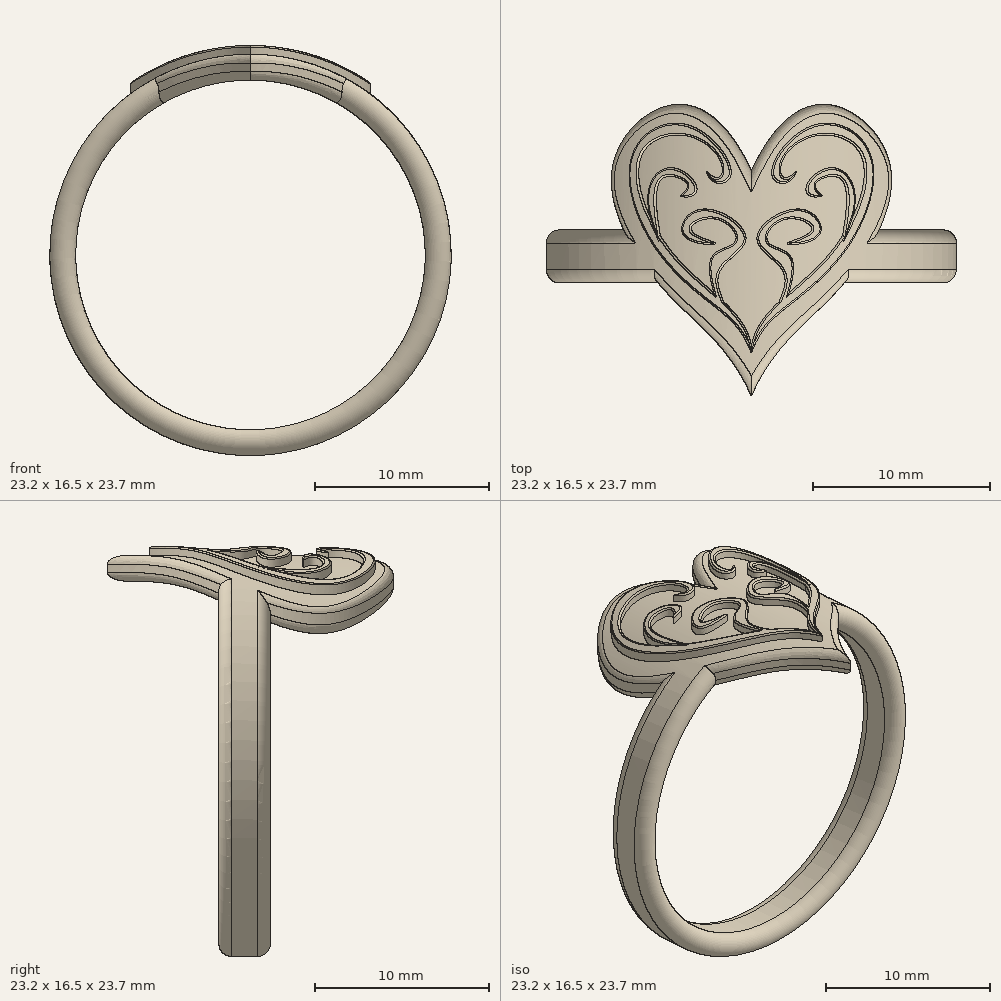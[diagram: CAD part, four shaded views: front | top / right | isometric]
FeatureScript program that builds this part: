
annotation { "Feature Type Name" : "Feature", "Feature Type Description" : "" }
export const myFeature = defineFeature(function(context is Context, id is Id, definition is map)
    precondition{}
    {
        {
            var Q0;
            Q0=qCreatedBy(makeId("Top.planeOp"),FACE);
            var sketch = newSketch(context, id + "F0", { "sketchPlane" : qUnion([Q0])});
            skFitSpline(sketch, "E0", {"points": [v(0, 4.84) * mm, v(-4.43, 8.58) * mm, v(-7.87, 5.02) * mm, v(-5.4, -1.36) * mm, v(-1.9, -4.93) * mm, v(0, -7.93) * mm], "startDerivative": vector(-17.19, 37.33) * mm, "endDerivative": vector(6.53, -16.13) * mm});
            skFitSpline(sketch, "E1.MirrorCS", {"points": [v(0, 4.84) * mm, v(4.43, 8.58) * mm, v(7.87, 5.02) * mm, v(5.4, -1.36) * mm, v(1.9, -4.93) * mm, v(0, -7.93) * mm], "startDerivative": vector(17.19, 37.33) * mm, "endDerivative": vector(-6.53, -16.13) * mm});
            skSolve(sketch);
        }
        {
            var Q0;
            Q0=qSketchRegion(id+"F0",true);
            extrude(context, id + "F1", {"entities" : qUnion([Q0]), "depth" : 19.05 * mm, "offsetDistance" : 25.4 * mm});
        }
        {
            var Q0;
            Q0=qCreatedBy(makeId("Front.planeOp"),FACE);
            var sketch = newSketch(context, id + "F2", { "sketchPlane" : qUnion([Q0])});
            skCircle(sketch, "E2", {"center": v(0, 0) * mm, "radius": 10.1 * mm});
            skCircle(sketch, "E3", {"center": v(0, 0) * mm, "radius": 11.6 * mm});
            skCircle(sketch, "E4", {"center": v(0, 0) * mm, "radius": 23.1 * mm});
            skCircle(sketch, "E5", {"center": v(0, 0) * mm, "radius": 12.1 * mm});
            skSolve(sketch);
        }
        {
            var Q0;
            Q0=makeQuery(id+"F2.imprint","IMPRINT",FACE,{"disambiguationData":[TD([[makeQuery(id+"F2.imprint","IMPRINT",EDGE,{"derivedFrom":sQuery(id+"F2.wireOp",EDGE,"E2")}),1.0]])]});
            extrude(context, id + "F3", {"entities" : qUnion([Q0]), "operationType" : NewBodyOperationType.REMOVE, "endBound" : BoundingType.SYMMETRIC, "oppositeDirection" : true, "depth" : 25.4 * mm, "offsetDistance" : 25.4 * mm});
        }
        {
            var Q0;
            Q0=makeQuery(id+"F2.imprint","IMPRINT",FACE,{"disambiguationData":[TD([[makeQuery(id+"F2.imprint","IMPRINT",EDGE,{"derivedFrom":sQuery(id+"F2.wireOp",EDGE,"J1NiXKZb-P4VB-i30b-1DHM-Y5gP9JKZlhvH")}),-1.0]])]});
            var Q1;
            Q1=makeQuery(id+"F2.imprint","IMPRINT",FACE,{"disambiguationData":[TD([[makeQuery(id+"F2.imprint","IMPRINT",EDGE,{"derivedFrom":sQuery(id+"F2.wireOp",EDGE,"E3")}),-1.0]])]});
            var Q2;
            Q2=makeQuery(id+"F2.imprint","IMPRINT",FACE,{"disambiguationData":[TD([[makeQuery(id+"F2.imprint","IMPRINT",EDGE,{"derivedFrom":sQuery(id+"F2.wireOp",EDGE,"E4")}),1.0]])]});
            extrude(context, id + "F4", {"entities" : qUnion([Q0, Q1, Q2]), "operationType" : NewBodyOperationType.REMOVE, "endBound" : BoundingType.SYMMETRIC, "oppositeDirection" : true, "depth" : 25.4 * mm, "offsetDistance" : 25.4 * mm});
        }
        {
            var Q0;
            Q0=makeQuery(id+"F2.imprint","IMPRINT",FACE,{"disambiguationData":[TD([[makeQuery(id+"F2.imprint","IMPRINT",EDGE,{"derivedFrom":sQuery(id+"F2.wireOp",EDGE,"E2")}),-1.0]])]});
            extrude(context, id + "F5", {"entities" : qUnion([Q0]), "operationType" : NewBodyOperationType.ADD, "endBound" : BoundingType.SYMMETRIC, "oppositeDirection" : true, "depth" : 3 * mm, "offsetDistance" : 25.4 * mm});
        }
        {
            var Q0;
            Q0=makeQuery(id+"F5.opExtrude","CAP_EDGE",EDGE,{"disambiguationData":[OSD([sQuery(id+"F2.wireOp",EDGE,"E3")])],"isStart":false});
            var Q1;
            Q1=makeQuery(id+"F5.opExtrude","CAP_EDGE",EDGE,{"disambiguationData":[OSD([sQuery(id+"F2.wireOp",EDGE,"E3")])],"isStart":true});
            var Q2;
            Q2=makeQuery(id+"F5.opExtrude","CAP_EDGE",EDGE,{"disambiguationData":[OSD([sQuery(id+"F2.wireOp",EDGE,"E2")])],"isStart":true});
            var Q3;
            Q3=makeQuery(id+"F5.opExtrude","CAP_EDGE",EDGE,{"disambiguationData":[OSD([sQuery(id+"F2.wireOp",EDGE,"E2")])],"isStart":false});
            fillet(context, id + "F6", {"entities" : qUnion([Q0, Q1, Q2, Q3]), "radius" : 0.75 * mm, "tangentPropagation" : true, "allowEdgeOverflow" : false});
        }
        {
            var Q0;
            {var subQ0=sQuery(id+"F2.wireOp",EDGE,"E2");Q0=makeQuery(id+"F3vgbqmcV8FAg6H_1.boolean.opBoolean","INTERSECT",EDGE,{"derivedFrom":[makeQuery(id+"F5.boolean.opBoolean","MERGE",FACE,{"derivedFrom":[makeQuery(id+"F3.boolean.opBoolean","COPY",FACE,{"derivedFrom":makeQuery(id+"F3.opExtrude","SWEPT_FACE",FACE,{"disambiguationData":[OSD([subQ0])]})}),makeQuery(id+"F5.opExtrude","SWEPT_FACE",FACE,{"disambiguationData":[OSD([subQ0])]})]}),makeQuery(id+"F3vgbqmcV8FAg6H_1.opExtrude","SWEPT_FACE",FACE,{"disambiguationData":[OSD([sQuery(id+"FdaOgL3yxnfuasM_1.wireOp",EDGE,"7c5b9e70-dd16-4398-a68a-3725518f416c")])]})]});}
            var Q1;
            {var subQ0=sQuery(id+"F2.wireOp",EDGE,"E3");Q1=makeQuery(id+"F3vgbqmcV8FAg6H_1.boolean.opBoolean","INTERSECT",EDGE,{"derivedFrom":[makeQuery(id+"F5.boolean.opBoolean","MERGE",FACE,{"derivedFrom":[makeQuery(id+"F4.boolean.opBoolean","COPY",FACE,{"derivedFrom":makeQuery(id+"F4.opExtrude","SWEPT_FACE",FACE,{"disambiguationData":[OSD([subQ0])]})}),makeQuery(id+"F5.opExtrude","SWEPT_FACE",FACE,{"disambiguationData":[OSD([subQ0])]})]}),makeQuery(id+"F3vgbqmcV8FAg6H_1.opExtrude","SWEPT_FACE",FACE,{"disambiguationData":[OSD([sQuery(id+"FdaOgL3yxnfuasM_1.wireOp",EDGE,"b2f0029b-c6ea-482f-b3c2-dee7be65e3070.MirrorCS")])]})]});}
            var Q2;
            {var subQ0=sQuery(id+"F2.wireOp",EDGE,"E2");Q2=makeQuery(id+"F3vgbqmcV8FAg6H_1.boolean.opBoolean","INTERSECT",EDGE,{"derivedFrom":[makeQuery(id+"F5.boolean.opBoolean","MERGE",FACE,{"derivedFrom":[makeQuery(id+"F3.boolean.opBoolean","COPY",FACE,{"derivedFrom":makeQuery(id+"F3.opExtrude","SWEPT_FACE",FACE,{"disambiguationData":[OSD([subQ0])]})}),makeQuery(id+"F5.opExtrude","SWEPT_FACE",FACE,{"disambiguationData":[OSD([subQ0])]})]}),makeQuery(id+"F3vgbqmcV8FAg6H_1.opExtrude","SWEPT_FACE",FACE,{"disambiguationData":[OSD([sQuery(id+"FdaOgL3yxnfuasM_1.wireOp",EDGE,"b2f0029b-c6ea-482f-b3c2-dee7be65e3070.MirrorCS")])]})]});}
            var Q3;
            {var subQ0=sQuery(id+"F2.wireOp",EDGE,"E3");Q3=makeQuery(id+"F3vgbqmcV8FAg6H_1.boolean.opBoolean","INTERSECT",EDGE,{"derivedFrom":[makeQuery(id+"F5.boolean.opBoolean","MERGE",FACE,{"derivedFrom":[makeQuery(id+"F4.boolean.opBoolean","COPY",FACE,{"derivedFrom":makeQuery(id+"F4.opExtrude","SWEPT_FACE",FACE,{"disambiguationData":[OSD([subQ0])]})}),makeQuery(id+"F5.opExtrude","SWEPT_FACE",FACE,{"disambiguationData":[OSD([subQ0])]})]}),makeQuery(id+"F3vgbqmcV8FAg6H_1.opExtrude","SWEPT_FACE",FACE,{"disambiguationData":[OSD([sQuery(id+"FdaOgL3yxnfuasM_1.wireOp",EDGE,"7c5b9e70-dd16-4398-a68a-3725518f416c")])]})]});}
            var Q4;
            {var subQ0=sQuery(id+"F2.wireOp",EDGE,"E3");var subQ1=makeQuery(id+"F4.opExtrude","SWEPT_FACE",FACE,{"disambiguationData":[OSD([subQ0])]});var subQ2=makeQuery(id+"F1.opExtrude","SWEPT_FACE",FACE,{"disambiguationData":[OSD([sQuery(id+"F0.wireOp",EDGE,"E0")])]});Q4=makeQuery(id+"F5.boolean.opBoolean","SPLIT",EDGE,{"disambiguationData":[TD([makeQuery(id+"F5.opExtrude","CAP_FACE",FACE,{"disambiguationData":[OSD([sQuery(id+"F2.wireOp",EDGE,"E2"),subQ0])],"isStart":false})])],"derivedFrom":makeQuery(id+"F4.boolean.opBoolean","INTERSECT",EDGE,{"derivedFrom":[subQ2,subQ1]})});}
            var Q5;
            {var subQ0=sQuery(id+"F2.wireOp",EDGE,"E3");var subQ1=makeQuery(id+"F4.opExtrude","SWEPT_FACE",FACE,{"disambiguationData":[OSD([subQ0])]});var subQ2=makeQuery(id+"F1.opExtrude","SWEPT_FACE",FACE,{"disambiguationData":[OSD([sQuery(id+"F0.wireOp",EDGE,"E1.MirrorCS")])]});Q5=makeQuery(id+"F5.boolean.opBoolean","SPLIT",EDGE,{"disambiguationData":[TD([makeQuery(id+"F5.opExtrude","CAP_FACE",FACE,{"disambiguationData":[OSD([sQuery(id+"F2.wireOp",EDGE,"E2"),subQ0])],"isStart":false})])],"derivedFrom":makeQuery(id+"F4.boolean.opBoolean","INTERSECT",EDGE,{"derivedFrom":[subQ2,subQ1]})});}
            var Q6;
            {var subQ0=sQuery(id+"F2.wireOp",EDGE,"E3");var subQ1=makeQuery(id+"F4.opExtrude","SWEPT_FACE",FACE,{"disambiguationData":[OSD([subQ0])]});var subQ2=makeQuery(id+"F1.opExtrude","SWEPT_FACE",FACE,{"disambiguationData":[OSD([sQuery(id+"F0.wireOp",EDGE,"E1.MirrorCS")])]});Q6=makeQuery(id+"F5.boolean.opBoolean","SPLIT",EDGE,{"disambiguationData":[TD([makeQuery(id+"F5.opExtrude","CAP_FACE",FACE,{"disambiguationData":[OSD([sQuery(id+"F2.wireOp",EDGE,"E2"),subQ0])],"isStart":true})])],"derivedFrom":makeQuery(id+"F4.boolean.opBoolean","INTERSECT",EDGE,{"derivedFrom":[subQ2,subQ1]})});}
            var Q7;
            {var subQ0=sQuery(id+"F2.wireOp",EDGE,"E3");var subQ1=makeQuery(id+"F4.opExtrude","SWEPT_FACE",FACE,{"disambiguationData":[OSD([subQ0])]});var subQ2=makeQuery(id+"F1.opExtrude","SWEPT_FACE",FACE,{"disambiguationData":[OSD([sQuery(id+"F0.wireOp",EDGE,"E0")])]});Q7=makeQuery(id+"F5.boolean.opBoolean","SPLIT",EDGE,{"disambiguationData":[TD([makeQuery(id+"F5.opExtrude","CAP_FACE",FACE,{"disambiguationData":[OSD([sQuery(id+"F2.wireOp",EDGE,"E2"),subQ0])],"isStart":true})])],"derivedFrom":makeQuery(id+"F4.boolean.opBoolean","INTERSECT",EDGE,{"derivedFrom":[subQ2,subQ1]})});}
            var Q8;
            {var subQ0=sQuery(id+"F2.wireOp",EDGE,"E2");var subQ1=makeQuery(id+"F3.opExtrude","SWEPT_FACE",FACE,{"disambiguationData":[OSD([subQ0])]});var subQ2=makeQuery(id+"F1.opExtrude","SWEPT_FACE",FACE,{"disambiguationData":[OSD([sQuery(id+"F0.wireOp",EDGE,"E0")])]});Q8=makeQuery(id+"F5.boolean.opBoolean","SPLIT",EDGE,{"disambiguationData":[TD([makeQuery(id+"F5.opExtrude","CAP_FACE",FACE,{"disambiguationData":[OSD([subQ0,sQuery(id+"F2.wireOp",EDGE,"E3")])],"isStart":true})])],"derivedFrom":makeQuery(id+"F3.boolean.opBoolean","INTERSECT",EDGE,{"derivedFrom":[subQ2,subQ1]})});}
            var Q9;
            {var subQ0=sQuery(id+"F2.wireOp",EDGE,"E2");var subQ1=makeQuery(id+"F3.opExtrude","SWEPT_FACE",FACE,{"disambiguationData":[OSD([subQ0])]});var subQ2=makeQuery(id+"F1.opExtrude","SWEPT_FACE",FACE,{"disambiguationData":[OSD([sQuery(id+"F0.wireOp",EDGE,"E1.MirrorCS")])]});Q9=makeQuery(id+"F5.boolean.opBoolean","SPLIT",EDGE,{"disambiguationData":[TD([makeQuery(id+"F5.opExtrude","CAP_FACE",FACE,{"disambiguationData":[OSD([subQ0,sQuery(id+"F2.wireOp",EDGE,"E3")])],"isStart":true})])],"derivedFrom":makeQuery(id+"F3.boolean.opBoolean","INTERSECT",EDGE,{"derivedFrom":[subQ2,subQ1]})});}
            var Q10;
            {var subQ0=sQuery(id+"F2.wireOp",EDGE,"E2");var subQ1=makeQuery(id+"F3.opExtrude","SWEPT_FACE",FACE,{"disambiguationData":[OSD([subQ0])]});var subQ2=makeQuery(id+"F1.opExtrude","SWEPT_FACE",FACE,{"disambiguationData":[OSD([sQuery(id+"F0.wireOp",EDGE,"E0")])]});Q10=makeQuery(id+"F5.boolean.opBoolean","SPLIT",EDGE,{"disambiguationData":[TD([makeQuery(id+"F5.opExtrude","CAP_FACE",FACE,{"disambiguationData":[OSD([subQ0,sQuery(id+"F2.wireOp",EDGE,"E3")])],"isStart":false})])],"derivedFrom":makeQuery(id+"F3.boolean.opBoolean","INTERSECT",EDGE,{"derivedFrom":[subQ2,subQ1]})});}
            var Q11;
            {var subQ0=sQuery(id+"F2.wireOp",EDGE,"E2");var subQ1=makeQuery(id+"F3.opExtrude","SWEPT_FACE",FACE,{"disambiguationData":[OSD([subQ0])]});var subQ2=makeQuery(id+"F1.opExtrude","SWEPT_FACE",FACE,{"disambiguationData":[OSD([sQuery(id+"F0.wireOp",EDGE,"E1.MirrorCS")])]});Q11=makeQuery(id+"F5.boolean.opBoolean","SPLIT",EDGE,{"disambiguationData":[TD([makeQuery(id+"F5.opExtrude","CAP_FACE",FACE,{"disambiguationData":[OSD([subQ0,sQuery(id+"F2.wireOp",EDGE,"E3")])],"isStart":false})])],"derivedFrom":makeQuery(id+"F3.boolean.opBoolean","INTERSECT",EDGE,{"derivedFrom":[subQ2,subQ1]})});}
            fillet(context, id + "F7", {"entities" : qUnion([Q0, Q1, Q2, Q3, Q4, Q5, Q6, Q7, Q8, Q9, Q10, Q11]), "radius" : 0.5 * mm, "tangentPropagation" : true, "allowEdgeOverflow" : false});
        }
        {
            var Q0;
            Q0=qCreatedBy(makeId("Top.planeOp"),FACE);
            var sketch = newSketch(context, id + "F8", { "sketchPlane" : qUnion([Q0])});
            skFitSpline(sketch, "E6", {"points": [v(0, -5.49) * mm, v(2.53, -2.5) * mm, v(5.77, 0.99) * mm, v(6.65, 5.95) * mm, v(3.46, 7.4) * mm, v(1.2, 4.44) * mm, v(2.58, 4.85) * mm], "startDerivative": vector(9.8, 27.27) * mm, "endDerivative": vector(7.73, 26.63) * mm});
            skFitSpline(sketch, "E7", {"points": [v(2.58, 4.85) * mm, v(1.65, 5) * mm, v(3.53, 6.79) * mm, v(6.17, 5.74) * mm, v(4.3, 0) * mm, v(0, -5.09) * mm], "startDerivative": vector(-21.25, -21.84) * mm, "endDerivative": vector(-3.33, -22.21) * mm});
            skFitSpline(sketch, "E8", {"points": [v(1.58, -2.56) * mm, v(1.79, -0.87) * mm, v(0.3, 1.03) * mm, v(2.91, 2.65) * mm, v(3.8, 1.14) * mm, v(2.02, 0.72) * mm, v(3.38, 1.45) * mm, v(2.02, 2.11) * mm, v(0.9, 0.87) * mm, v(2.22, 0) * mm, v(2.13, -2.06) * mm], "startDerivative": vector(5.29, 13.81) * mm, "endDerivative": vector(-3.15, -11.95) * mm});
            skFitSpline(sketch, "E9", {"points": [v(5.69, 2.13) * mm, v(4.62, 5.02) * mm, v(3.1, 3.92) * mm, v(4.06, 3.4) * mm], "startDerivative": vector(3.8, 11.9) * mm, "endDerivative": vector(9.14, 1.92) * mm});
            skFitSpline(sketch, "E10", {"points": [v(4.06, 3.4) * mm, v(3.7, 4.16) * mm, v(4.89, 4.47) * mm, v(5.15, 1.15) * mm], "startDerivative": vector(-5.46, 3.97) * mm, "endDerivative": vector(-2.1, -11.43) * mm});
            skFitSpline(sketch, "E11.MirrorCS", {"points": [v(-1.58, -2.56) * mm, v(-1.79, -0.87) * mm, v(-0.3, 1.03) * mm, v(-2.91, 2.65) * mm, v(-3.8, 1.14) * mm, v(-2.02, 0.72) * mm, v(-3.38, 1.45) * mm, v(-2.02, 2.11) * mm, v(-0.9, 0.87) * mm, v(-2.22, 0) * mm, v(-2.13, -2.06) * mm], "startDerivative": vector(-5.29, 13.81) * mm, "endDerivative": vector(3.15, -11.95) * mm});
            skFitSpline(sketch, "E12.MirrorCS", {"points": [v(0, -5.49) * mm, v(-2.53, -2.5) * mm, v(-5.77, 0.99) * mm, v(-6.65, 5.95) * mm, v(-3.46, 7.4) * mm, v(-1.2, 4.44) * mm, v(-2.58, 4.85) * mm], "startDerivative": vector(-9.8, 27.27) * mm, "endDerivative": vector(-7.73, 26.63) * mm});
            skFitSpline(sketch, "E13.MirrorCS", {"points": [v(-2.58, 4.85) * mm, v(-1.65, 5) * mm, v(-3.53, 6.79) * mm, v(-6.17, 5.74) * mm, v(-4.3, 0) * mm, v(0, -5.09) * mm], "startDerivative": vector(21.25, -21.84) * mm, "endDerivative": vector(3.33, -22.21) * mm});
            skFitSpline(sketch, "E14.MirrorCS", {"points": [v(-4.06, 3.4) * mm, v(-3.7, 4.16) * mm, v(-4.89, 4.47) * mm, v(-5.15, 1.15) * mm], "startDerivative": vector(5.46, 3.97) * mm, "endDerivative": vector(2.1, -11.43) * mm});
            skFitSpline(sketch, "E15.MirrorCS", {"points": [v(-5.69, 2.13) * mm, v(-4.62, 5.02) * mm, v(-3.1, 3.92) * mm, v(-4.06, 3.4) * mm], "startDerivative": vector(-3.8, 11.9) * mm, "endDerivative": vector(-9.14, 1.92) * mm});
            skSolve(sketch);
        }
        {
            var Q0;
            Q0 = qSketchRegion(id + "F8", true);
            extrude(context, id + "F9", {"entities" : qUnion([Q0]), "operationType" : NewBodyOperationType.ADD, "depth" : 19.05 * mm, "offsetDistance" : 25.4 * mm});
        }
        {
            var Q0;
            Q0=makeQuery(id+"F2.imprint","IMPRINT",FACE,{"disambiguationData":[TD([[makeQuery(id+"F2.imprint","IMPRINT",EDGE,{"derivedFrom":sQuery(id+"F2.wireOp",EDGE,"E2")}),1.0]])]});
            var Q1;
            Q1=makeQuery(id+"F2.imprint","IMPRINT",FACE,{"disambiguationData":[TD([[makeQuery(id+"F2.imprint","IMPRINT",EDGE,{"derivedFrom":sQuery(id+"F2.wireOp",EDGE,"E4")}),1.0]])]});
            extrude(context, id + "F10", {"entities" : qUnion([Q0, Q1]), "operationType" : NewBodyOperationType.REMOVE, "endBound" : BoundingType.SYMMETRIC, "oppositeDirection" : true, "depth" : 25.4 * mm, "offsetDistance" : 25.4 * mm});
        }
        {
            var Q0;
            Q0=makeQuery(id+"F10.boolean.opBoolean","COPY",FACE,{"derivedFrom":makeQuery(id+"F10.opExtrude","SWEPT_FACE",FACE,{"disambiguationData":[OSD([sQuery(id+"F2.wireOp",EDGE,"E5")])]})});
            fillet(context, id + "F11", {"entities" : qUnion([Q0]), "radius" : 0.1 * mm, "tangentPropagation" : true, "allowEdgeOverflow" : false});
        }
    });
